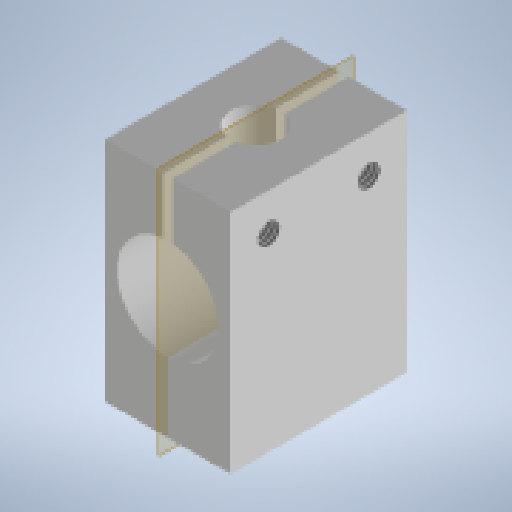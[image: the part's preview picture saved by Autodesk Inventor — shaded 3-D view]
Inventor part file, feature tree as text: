
AUTODESK INVENTOR PART (.ipt)
format: ipt  version: 2024.2 (Build 282272000, 272)  size: 314,880 bytes
history: native  units: mm
features: extrude x9, sketch x4, thread x2, hole x1, plane x1
ambient origin geometry x8: Origin, YZ Plane, XZ Plane, XY Plane, X Axis, Y Axis, Z Axis, Center Point
bodies: Solid1 (feature_tree)
feature tree (17):
  extrude  "Extrusion1"  Depth=36.1mm
  extrude  "Extrusion2"  Depth=10.0mm
  extrude  "Extrusion3"  Depth=19.1mm
  extrude  "Extrusion4"  Depth=29.622mm
  extrude  "Extrusion5"  Depth=29.622mm
  extrude  "Extrusion8"  Depth=29.622mm
  thread  "Thread8"  [1 undecoded]
  thread  "Thread11"  [1 undecoded]
  hole  "Hole1"  [1 undecoded]
  extrude  "Extrusion12"  Depth=29.622mm
  extrude  "Extrusion13"  Depth=10.0mm TaperAngle=0.0deg
  extrude  "Extrusion14"  Depth=29.622mm
  plane  "Work Plane1"
  sketch  "Sketch1"  dims[d0=20.0mm d1=36.1mm]
  sketch  "Sketch3"  dims[d2=28.0mm d3=0.0mm d4=10.0mm]
  sketch  "Sketch11"  dims[d5=16.1mm d6=19.1mm]
  sketch  "Sketch13"  dims[d7=30.0mm d8=0.0mm d9=18.0mm d11=1.5mm d12=0.75mm d13=30.0mm d14=0.0mm d15=14.0mm d16=10.0mm d17=4.572mm d18=10.0mm d19=0.0mm d20=6.0mm d21=6.0mm d22=4.98mm d23=4.98mm d24=6.0mm d25=6.0mm d26=10.0mm d27=0.0mm d28=3.45mm d29=3.45mm d34=10.0mm d35=0.0mm d61=10.0mm d62=0.0mm d67=10.0mm d68=0.0mm d69=5.0mm d71=2.02184mm d74=2.02184mm d75=6.0mm d76=4.0mm d77=2.0mm d78=90.0deg d79=1.91mm d80=20.594885mm d81=0.5mm d82=2.02184mm d83=1.91mm d84=0.0mm d88=6.0mm d89=6.0mm d91=6.0mm d92=6.0mm d93=7.9375mm d94=7.9375mm d95=4.572mm d96=0.0mm d97=10.0mm d98=7.9375mm d99=29.622mm d100=0.0mm d85=0.375mm]
note: 3 required parameter values undecoded (feature->parameter linkage not recoverable at this tier; creation-order binding heuristic only, values carry confidence <= 0.55)
